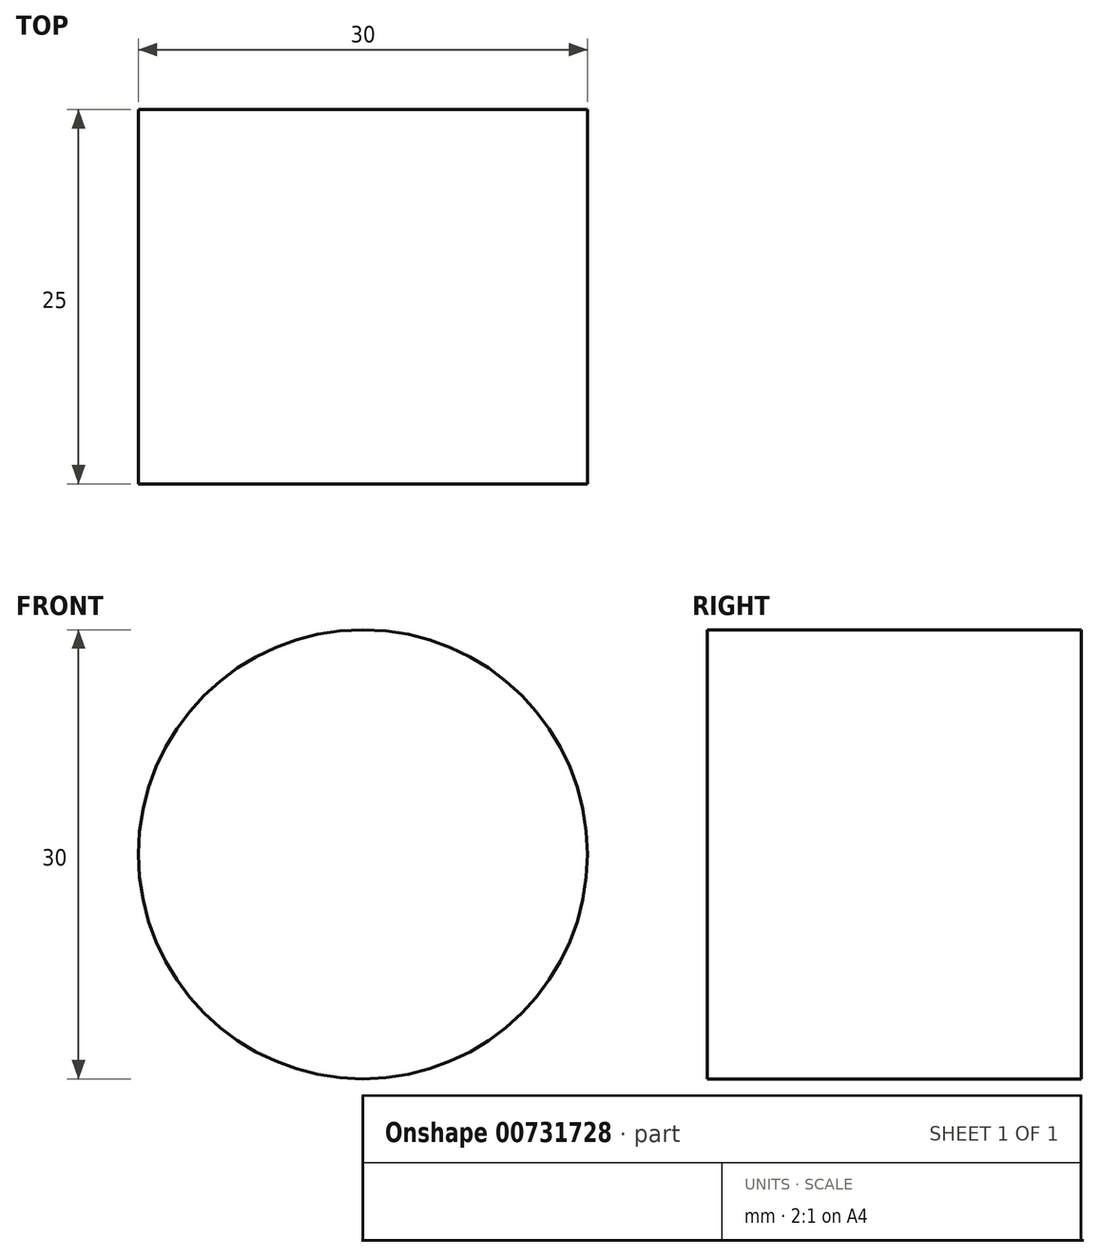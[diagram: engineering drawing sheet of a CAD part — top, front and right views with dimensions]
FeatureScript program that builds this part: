
annotation { "Feature Type Name" : "Feature", "Feature Type Description" : "" }
export const myFeature = defineFeature(function(context is Context, id is Id, definition is map)
    precondition{}
    {
        {
            var Q0;
            Q0=qCreatedBy(makeId("Front.planeOp"),FACE);
            var sketch = newSketch(context, id + "F0", { "sketchPlane" : qUnion([Q0])});
            skCircle(sketch, "E0", {"center": v(0, 0) * mm, "radius": 15 * mm});
            skSolve(sketch);
        }
        {
            var Q0;
            Q0=makeQuery(id+"F0.imprint","IMPRINT",FACE,{"disambiguationData":[TD([[makeQuery(id+"F0.imprint","IMPRINT",EDGE,{"derivedFrom":sQuery(id+"F0.wireOp",EDGE,"E0")}),1.0]])]});
            extrude(context, id + "F1", {"entities" : qUnion([Q0]), "depth" : 25 * mm, "offsetDistance" : 25 * mm});
        }
    });
